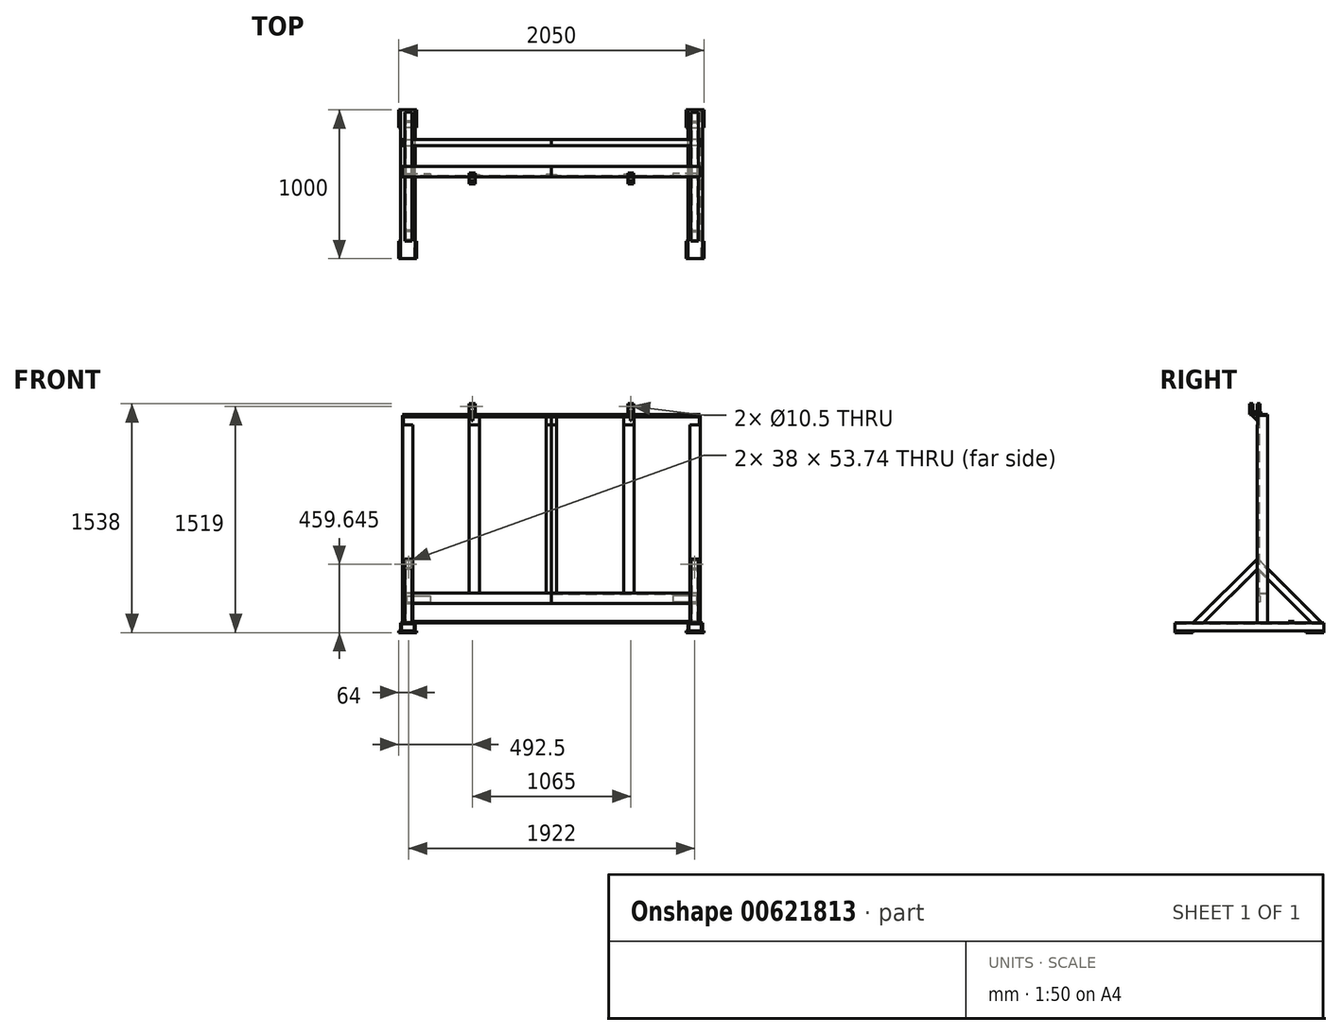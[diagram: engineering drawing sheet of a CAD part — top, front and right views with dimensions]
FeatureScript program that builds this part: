
annotation { "Feature Type Name" : "Feature", "Feature Type Description" : "" }
export const myFeature = defineFeature(function(context is Context, id is Id, definition is map)
    precondition{}
    {
        {
            var Q0;
            Q0=qCreatedBy(makeId("Front.planeOp"),FACE);
            var sketch = newSketch(context, id + "F0", { "sketchPlane" : qUnion([Q0])});
            skLineSegment(sketch, "E0", {"start": v(-915, 0) * mm, "end": v(-915, 53) * mm});
            skLineSegment(sketch, "E1", {"start": v(-915, 53) * mm, "end": v(-1015, 53) * mm});
            skLineSegment(sketch, "E2", {"start": v(-1015, 53) * mm, "end": v(-1015, 0) * mm});
            skLineSegment(sketch, "E3", {"start": v(-1015, 0) * mm, "end": v(-1007, 0) * mm});
            skLineSegment(sketch, "E4", {"start": v(-1007, 0) * mm, "end": v(-1007, 47) * mm});
            skLineSegment(sketch, "E5", {"start": v(-1007, 47) * mm, "end": v(-923, 47) * mm});
            skLineSegment(sketch, "E6", {"start": v(-923, 47) * mm, "end": v(-923, 0) * mm});
            skLineSegment(sketch, "E7", {"start": v(-923, 0) * mm, "end": v(-915, 0) * mm});
            skLineSegment(sketch, "E8", {"start": v(0, 0) * mm, "end": v(0, 53) * mm, "construction": true});
            skSolve(sketch);
        }
        {
            var Q0;
            Q0=qSketchRegion(id+"F0",true);
            extrude(context, id + "F1", {"entities" : qUnion([Q0]), "depth" : 1000 * mm, "hasSecondDirection" : true, "secondDirectionOppositeDirection" : true, "secondDirectionDepth" : 500 * mm, "symmetric" : true});
        }
        {
            var Q0;
            Q0=makeQuery(id+"F1.opExtrude","SWEPT_FACE",FACE,{"disambiguationData":[OSD([sQuery(id+"F0.wireOp",EDGE,"E1")])]});
            var sketch = newSketch(context, id + "F2", { "sketchPlane" : qUnion([Q0])});
            skLineSegment(sketch, "E9", {"start": v(-965, -500) * mm, "end": v(-965, 500) * mm, "construction": true});
            skLineSegment(sketch, "E10", {"start": v(-930, 50) * mm, "end": v(-1000, 50) * mm});
            skLineSegment(sketch, "E11", {"start": v(-1000, 50) * mm, "end": v(-1000, 120) * mm});
            skLineSegment(sketch, "E12", {"start": v(-1000, 120) * mm, "end": v(-994, 120) * mm});
            skLineSegment(sketch, "E13", {"start": v(-994, 120) * mm, "end": v(-994, 56) * mm});
            skLineSegment(sketch, "E14", {"start": v(-994, 56) * mm, "end": v(-930, 56) * mm});
            skLineSegment(sketch, "E15", {"start": v(-930, 56) * mm, "end": v(-930, 50) * mm});
            skSolve(sketch);
        }
        {
            var Q0;
            Q0=qSketchRegion(id+"F2",true);
            extrude(context, id + "F3", {"entities" : qUnion([Q0]), "depth" : 1400 * mm});
        }
        {
            var Q0;
            Q0=makeQuery(id+"F3.opExtrude","SWEPT_FACE",FACE,{"disambiguationData":[OSD([sQuery(id+"F2.wireOp",EDGE,"E10")])]});
            var sketch = newSketch(context, id + "F4", { "sketchPlane" : qUnion([Q0])});
            skLineSegment(sketch, "E16", {"start": v(-1000, 1453) * mm, "end": v(-930, 1383) * mm});
            skLineSegment(sketch, "E17", {"start": v(-930, 1383) * mm, "end": v(-930, 1453) * mm});
            skLineSegment(sketch, "E18", {"start": v(-930, 1453) * mm, "end": v(-1000, 1453) * mm});
            skSolve(sketch);
        }
        {
            var Q0;
            Q0=makeQuery(id+"F4.imprint","IMPRINT",FACE,{"disambiguationData":[TD([[makeQuery(id+"F4.imprint","IMPRINT",EDGE,{"derivedFrom":sQuery(id+"F4.wireOp",EDGE,"E16")}),1.0]])]});
            extrude(context, id + "F5", {"entities" : qUnion([Q0]), "operationType" : NewBodyOperationType.REMOVE, "endBound" : BoundingType.UP_TO_NEXT, "oppositeDirection" : true, "depth" : 25 * mm});
        }
        {
            var Q0;
            Q0=makeQuery(id+"F3.opExtrude","SWEPT_FACE",FACE,{"disambiguationData":[OSD([sQuery(id+"F2.wireOp",EDGE,"E11")])]});
            var sketch = newSketch(context, id + "F6", { "sketchPlane" : qUnion([Q0])});
            skLineSegment(sketch, "E19", {"start": v(-120, 1453) * mm, "end": v(-50, 1453) * mm});
            skLineSegment(sketch, "E20", {"start": v(-50, 1453) * mm, "end": v(-50, 1383) * mm});
            skLineSegment(sketch, "E21", {"start": v(-50, 1383) * mm, "end": v(-56, 1383) * mm});
            skLineSegment(sketch, "E22", {"start": v(-56, 1383) * mm, "end": v(-56, 1447) * mm});
            skLineSegment(sketch, "E23", {"start": v(-56, 1447) * mm, "end": v(-120, 1447) * mm});
            skLineSegment(sketch, "E24", {"start": v(-120, 1447) * mm, "end": v(-120, 1453) * mm});
            skSolve(sketch);
        }
        {
            var Q0;
            Q0=makeQuery(id+"F6.imprint","IMPRINT",FACE,{"disambiguationData":[TD([[makeQuery(id+"F6.imprint","IMPRINT",EDGE,{"derivedFrom":sQuery(id+"F6.wireOp",EDGE,"E19")}),1.0]])]});
            var Q1;
            Q1=qCreatedBy(makeId("Right.planeOp"),FACE);
            extrude(context, id + "F7", {"entities" : qUnion([Q0]), "endBound" : BoundingType.UP_TO_SURFACE, "oppositeDirection" : true, "endBoundEntityFace" : qUnion([Q1]), "depth" : 1105 * mm});
        }
        {
            var Q0;
            Q0=makeQuery(id+"F7.opExtrude","SWEPT_FACE",FACE,{"disambiguationData":[OSD([sQuery(id+"F6.wireOp",EDGE,"E20")])]});
            var sketch = newSketch(context, id + "F8", { "sketchPlane" : qUnion([Q0])});
            skLineSegment(sketch, "E25", {"start": v(-1000, 1453) * mm, "end": v(-1000, 1383) * mm});
            skLineSegment(sketch, "E26", {"start": v(-1000, 1383) * mm, "end": v(-930, 1383) * mm});
            skLineSegment(sketch, "E27", {"start": v(-930, 1383) * mm, "end": v(-1000, 1453) * mm});
            skSolve(sketch);
        }
        {
            var Q0;
            Q0=makeQuery(id+"F8.imprint","IMPRINT",FACE,{"disambiguationData":[TD([[makeQuery(id+"F8.imprint","IMPRINT",EDGE,{"derivedFrom":sQuery(id+"F8.wireOp",EDGE,"E25")}),1.0]])]});
            extrude(context, id + "F9", {"entities" : qUnion([Q0]), "operationType" : NewBodyOperationType.REMOVE, "endBound" : BoundingType.UP_TO_NEXT, "oppositeDirection" : true, "depth" : 25 * mm});
        }
        {
            var Q0;
            Q0=makeQuery(id+"F3.opExtrude","SWEPT_FACE",FACE,{"disambiguationData":[OSD([sQuery(id+"F2.wireOp",EDGE,"E13")])]});
            cPlane(context, id + "F10", {"entities" : qUnion([Q0]), "cplaneType" : CPlaneType.OFFSET, "offset" : 8 * mm, "width" : 150 * mm, "height" : 150 * mm});
        }
        {
            var Q0;
            Q0=qCreatedBy(id+"F10.planeOp",FACE);
            var sketch = newSketch(context, id + "F11", { "sketchPlane" : qUnion([Q0])});
            skLineSegment(sketch, "E28", {"start": v(56, 483) * mm, "end": v(56, 412.29) * mm});
            skLineSegment(sketch, "E29", {"start": v(56, 412.29) * mm, "end": v(415.29, 53) * mm});
            skLineSegment(sketch, "E30", {"start": v(415.29, 53) * mm, "end": v(486, 53) * mm});
            skLineSegment(sketch, "E31", {"start": v(486, 53) * mm, "end": v(56, 483) * mm});
            skLineSegment(sketch, "E32", {"start": v(50, 483) * mm, "end": v(-380, 53) * mm});
            skLineSegment(sketch, "E33", {"start": v(-380, 53) * mm, "end": v(-309.29, 53) * mm});
            skLineSegment(sketch, "E34", {"start": v(-309.29, 53) * mm, "end": v(50, 412.29) * mm});
            skLineSegment(sketch, "E35", {"start": v(50, 412.29) * mm, "end": v(50, 483) * mm});
            skSolve(sketch);
        }
        {
            var Q0;
            Q0=qSketchRegion(id+"F11",true);
            extrude(context, id + "F12", {"entities" : qUnion([Q0]), "depth" : 50 * mm});
        }
        {
            var Q0;
            Q0=makeQuery(id+"F12.opExtrude","SWEPT_FACE",FACE,{"disambiguationData":[OSD([sQuery(id+"F11.wireOp",EDGE,"E33")])]});
            var Q1;
            Q1=makeQuery(id+"F12.opExtrude","SWEPT_FACE",FACE,{"disambiguationData":[OSD([sQuery(id+"F11.wireOp",EDGE,"E30")])]});
            var Q2;
            Q2=makeQuery(id+"F12.opExtrude","SWEPT_FACE",FACE,{"disambiguationData":[OSD([sQuery(id+"F11.wireOp",EDGE,"E28")])]});
            var Q3;
            Q3=makeQuery(id+"F12.opExtrude","SWEPT_FACE",FACE,{"disambiguationData":[OSD([sQuery(id+"F11.wireOp",EDGE,"E35")])]});
            shell(context, id + "F13", {"entities" : qUnion([Q0, Q1, Q2, Q3]), "thickness" : 6 * mm});
        }
        {
            var Q0;
            Q0=makeQuery(id+"F3.opExtrude","SWEPT_FACE",FACE,{"disambiguationData":[OSD([sQuery(id+"F2.wireOp",EDGE,"E13")])]});
            var sketch = newSketch(context, id + "F14", { "sketchPlane" : qUnion([Q0])});
            skLineSegment(sketch, "E36", {"start": v(50, 253) * mm, "end": v(120, 253) * mm});
            skLineSegment(sketch, "E37", {"start": v(120, 253) * mm, "end": v(120, 247) * mm});
            skLineSegment(sketch, "E38", {"start": v(120, 247) * mm, "end": v(56, 247) * mm});
            skLineSegment(sketch, "E39", {"start": v(56, 247) * mm, "end": v(56, 183) * mm});
            skLineSegment(sketch, "E40", {"start": v(56, 183) * mm, "end": v(50, 183) * mm});
            skLineSegment(sketch, "E41", {"start": v(50, 183) * mm, "end": v(50, 253) * mm});
            skSolve(sketch);
        }
        {
            var Q0;
            {var subQ1=sQuery(id+"F14.wireOp",EDGE,"E39");Q0=makeQuery(id+"F14.imprint","IMPRINT",FACE,{"disambiguationData":[TD([[makeQuery(id+"F14.imprint","IMPRINT",EDGE,{"derivedFrom":subQ1}),-1.0]])]});}
            var Q1;
            {var subQ0=sQuery(id+"F14.wireOp",EDGE,"E37");Q1=makeQuery(id+"F14.imprint","IMPRINT",FACE,{"disambiguationData":[TD([[makeQuery(id+"F14.imprint","IMPRINT",EDGE,{"derivedFrom":subQ0}),-1.0]])]});}
            var Q2;
            Q2=qCreatedBy(makeId("Right.planeOp"),FACE);
            var Q3;
            Q3=makeQuery(id+"F7.opExtrude","SWEPT_BODY",BODY,{"disambiguationData":[OSD([sQuery(id+"F6.wireOp",EDGE,"E19"),sQuery(id+"F6.wireOp",EDGE,"E20"),sQuery(id+"F6.wireOp",EDGE,"E21"),sQuery(id+"F6.wireOp",EDGE,"E22"),sQuery(id+"F6.wireOp",EDGE,"E23"),sQuery(id+"F6.wireOp",EDGE,"E24")])]});
            extrude(context, id + "F15", {"entities" : qUnion([Q0, Q1]), "endBound" : BoundingType.UP_TO_SURFACE, "endBoundEntityFace" : qUnion([Q2]), "endBoundEntityBody" : qUnion([Q3]), "depth" : 1005 * mm});
        }
        {
            var Q0;
            Q0=makeQuery(id+"F15.opExtrude","SWEPT_FACE",FACE,{"disambiguationData":[OSD([sQuery(id+"F14.wireOp",EDGE,"E41")])]});
            var sketch = newSketch(context, id + "F16", { "sketchPlane" : qUnion([Q0])});
            skLineSegment(sketch, "E42.bottom", {"start": v(-994, 253) * mm, "end": v(-930, 253) * mm});
            skLineSegment(sketch, "E42.top", {"start": v(-994, 183) * mm, "end": v(-930, 183) * mm});
            skLineSegment(sketch, "E42.left", {"start": v(-994, 253) * mm, "end": v(-994, 183) * mm});
            skLineSegment(sketch, "E42.right", {"start": v(-930, 253) * mm, "end": v(-930, 183) * mm});
            skSolve(sketch);
        }
        {
            var Q0;
            Q0=makeQuery(id+"F16.imprint","IMPRINT",FACE,{"disambiguationData":[TD([[makeQuery(id+"F16.imprint","IMPRINT",EDGE,{"derivedFrom":sQuery(id+"F16.wireOp",EDGE,"E42.bottom")}),1.0]])]});
            extrude(context, id + "F17", {"entities" : qUnion([Q0]), "operationType" : NewBodyOperationType.REMOVE, "oppositeDirection" : true, "depth" : 70 * mm});
        }
        {
            var Q0;
            Q0=makeQuery(id+"F3.opExtrude","SWEPT_FACE",FACE,{"disambiguationData":[OSD([sQuery(id+"F2.wireOp",EDGE,"E14")])]});
            var sketch = newSketch(context, id + "F18", { "sketchPlane" : qUnion([Q0])});
            skLineSegment(sketch, "E43.bottom", {"start": v(974, 235) * mm, "end": v(814, 235) * mm});
            skLineSegment(sketch, "E43.top", {"start": v(974, 195) * mm, "end": v(814, 195) * mm});
            skLineSegment(sketch, "E43.left", {"start": v(974, 235) * mm, "end": v(974, 195) * mm});
            skLineSegment(sketch, "E43.right", {"start": v(814, 235) * mm, "end": v(814, 195) * mm});
            skLineSegment(sketch, "E44", {"start": v(814, 215) * mm, "end": v(974, 215) * mm, "construction": true});
            skSolve(sketch);
        }
        {
            var Q0;
            {var subQ0=sQuery(id+"F18.wireOp",EDGE,"E43.right");Q0=makeQuery(id+"F18.imprint","IMPRINT",FACE,{"disambiguationData":[TD([[makeQuery(id+"F18.imprint","IMPRINT",EDGE,{"derivedFrom":subQ0}),1.0]])]});}
            var Q1;
            {var subQ0=sQuery(id+"F18.wireOp",EDGE,"E43.left");Q1=makeQuery(id+"F18.imprint","IMPRINT",FACE,{"disambiguationData":[TD([[makeQuery(id+"F18.imprint","IMPRINT",EDGE,{"derivedFrom":subQ0}),-1.0]])]});}
            extrude(context, id + "F19", {"entities" : qUnion([Q0, Q1]), "depth" : 15 * mm});
        }
        {
            var Q0;
            Q0=makeQuery(id+"F7.opExtrude","SWEPT_FACE",FACE,{"disambiguationData":[OSD([sQuery(id+"F6.wireOp",EDGE,"E20")])]});
            var sketch = newSketch(context, id + "F20", { "sketchPlane" : qUnion([Q0])});
            skLineSegment(sketch, "E45.bottom", {"start": v(0, 1438) * mm, "end": v(-35, 1438) * mm});
            skLineSegment(sketch, "E45.top", {"start": v(0, 253) * mm, "end": v(-35, 253) * mm});
            skLineSegment(sketch, "E45.left", {"start": v(0, 1438) * mm, "end": v(0, 253) * mm});
            skLineSegment(sketch, "E45.right", {"start": v(-35, 1438) * mm, "end": v(-35, 253) * mm});
            skLineSegment(sketch, "E46.bottom", {"start": v(-555, 1438) * mm, "end": v(-485, 1438) * mm});
            skLineSegment(sketch, "E46.top", {"start": v(-555, 253) * mm, "end": v(-485, 253) * mm});
            skLineSegment(sketch, "E46.left", {"start": v(-555, 1438) * mm, "end": v(-555, 253) * mm});
            skLineSegment(sketch, "E46.right", {"start": v(-485, 1438) * mm, "end": v(-485, 253) * mm});
            skSolve(sketch);
        }
        {
            var Q0;
            {var subQ0=sQuery(id+"F20.wireOp",EDGE,"E46.bottom");Q0=makeQuery(id+"F20.imprint","IMPRINT",FACE,{"disambiguationData":[TD([[makeQuery(id+"F20.imprint","IMPRINT",EDGE,{"derivedFrom":subQ0}),-1.0]])]});}
            var Q1;
            {var subQ0=sQuery(id+"F20.wireOp",EDGE,"E46.top");Q1=makeQuery(id+"F20.imprint","IMPRINT",FACE,{"disambiguationData":[TD([[makeQuery(id+"F20.imprint","IMPRINT",EDGE,{"derivedFrom":subQ0}),1.0]])]});}
            var Q2;
            {var subQ0=sQuery(id+"F20.wireOp",EDGE,"E45.bottom");Q2=makeQuery(id+"F20.imprint","IMPRINT",FACE,{"disambiguationData":[TD([[makeQuery(id+"F20.imprint","IMPRINT",EDGE,{"derivedFrom":subQ0}),1.0]])]});}
            var Q3;
            {var subQ0=sQuery(id+"F20.wireOp",EDGE,"E45.top");Q3=makeQuery(id+"F20.imprint","IMPRINT",FACE,{"disambiguationData":[TD([[makeQuery(id+"F20.imprint","IMPRINT",EDGE,{"derivedFrom":subQ0}),-1.0]])]});}
            extrude(context, id + "F21", {"entities" : qUnion([Q0, Q1, Q2, Q3]), "oppositeDirection" : true, "depth" : 15 * mm});
        }
        {
            var Q0;
            Q0=makeQuery(id+"F21.opExtrude","SWEPT_FACE",FACE,{"disambiguationData":[OSD([sQuery(id+"F20.wireOp",EDGE,"E45.left")])]});
            var sketch = newSketch(context, id + "F22", { "sketchPlane" : qUnion([Q0])});
            skLineSegment(sketch, "E47.bottom", {"start": v(56, 1438) * mm, "end": v(50, 1438) * mm});
            skLineSegment(sketch, "E47.top", {"start": v(56, 1383) * mm, "end": v(50, 1383) * mm});
            skLineSegment(sketch, "E47.left", {"start": v(56, 1438) * mm, "end": v(56, 1383) * mm});
            skLineSegment(sketch, "E47.right", {"start": v(50, 1438) * mm, "end": v(50, 1383) * mm});
            skSolve(sketch);
        }
        {
            var Q0;
            Q0=makeQuery(id+"F22.imprint","IMPRINT",FACE,{"disambiguationData":[TD([[makeQuery(id+"F22.imprint","IMPRINT",EDGE,{"derivedFrom":sQuery(id+"F22.wireOp",EDGE,"E47.bottom")}),1.0]])]});
            extrude(context, id + "F23", {"entities" : qUnion([Q0]), "operationType" : NewBodyOperationType.REMOVE, "oppositeDirection" : true, "depth" : 1000 * mm});
        }
        {
            var Q0;
            Q0=makeQuery(id+"F1.opExtrude","SWEPT_FACE",FACE,{"disambiguationData":[OSD([sQuery(id+"F0.wireOp",EDGE,"E1")])]});
            var sketch = newSketch(context, id + "F24", { "sketchPlane" : qUnion([Q0])});
            skLineSegment(sketch, "E48.bottom", {"start": v(-1005, 260) * mm, "end": v(0, 260) * mm});
            skLineSegment(sketch, "E48.top", {"start": v(-1005, 300) * mm, "end": v(0, 300) * mm});
            skLineSegment(sketch, "E48.left", {"start": v(-1005, 260) * mm, "end": v(-1005, 300) * mm});
            skLineSegment(sketch, "E48.right", {"start": v(0, 260) * mm, "end": v(0, 300) * mm});
            skSolve(sketch);
        }
        {
            var Q0;
            {var subQ0=sQuery(id+"F24.wireOp",EDGE,"E48.right");Q0=makeQuery(id+"F24.imprint","IMPRINT",FACE,{"disambiguationData":[TD([[makeQuery(id+"F24.imprint","IMPRINT",EDGE,{"derivedFrom":subQ0}),1.0]])]});}
            var Q1;
            {var subQ0=sQuery(id+"F24.wireOp",EDGE,"E48.left");Q1=makeQuery(id+"F24.imprint","IMPRINT",FACE,{"disambiguationData":[TD([[makeQuery(id+"F24.imprint","IMPRINT",EDGE,{"derivedFrom":subQ0}),-1.0]])]});}
            extrude(context, id + "F25", {"entities" : qUnion([Q0, Q1]), "depth" : 12 * mm});
        }
        {
            var Q0;
            Q0=makeQuery(id+"F7.opExtrude","SWEPT_FACE",FACE,{"disambiguationData":[OSD([sQuery(id+"F6.wireOp",EDGE,"E19")])]});
            var sketch = newSketch(context, id + "F26", { "sketchPlane" : qUnion([Q0])});
            skLineSegment(sketch, "E49.bottom", {"start": v(-552.5, 77) * mm, "end": v(-512.5, 77) * mm});
            skLineSegment(sketch, "E49.top", {"start": v(-552.5, 2) * mm, "end": v(-512.5, 2) * mm});
            skLineSegment(sketch, "E49.left", {"start": v(-552.5, 77) * mm, "end": v(-552.5, 2) * mm});
            skLineSegment(sketch, "E49.right", {"start": v(-512.5, 77) * mm, "end": v(-512.5, 2) * mm});
            skSolve(sketch);
        }
        {
            var Q0;
            Q0=qSketchRegion(id+"F26",true);
            extrude(context, id + "F27", {"entities" : qUnion([Q0]), "depth" : 20 * mm});
        }
        {
            var Q0;
            Q0=makeQuery(id+"F27.opExtrude","CAP_FACE",FACE,{"disambiguationData":[OSD([sQuery(id+"F26.wireOp",EDGE,"E49.bottom"),sQuery(id+"F26.wireOp",EDGE,"E49.top"),sQuery(id+"F26.wireOp",EDGE,"E49.left"),sQuery(id+"F26.wireOp",EDGE,"E49.right")])],"isStart":false});
            var sketch = newSketch(context, id + "F28", { "sketchPlane" : qUnion([Q0])});
            skLineSegment(sketch, "E50.bottom", {"start": v(-552.5, 2) * mm, "end": v(-512.5, 2) * mm});
            skLineSegment(sketch, "E50.top", {"start": v(-552.5, 22) * mm, "end": v(-512.5, 22) * mm});
            skLineSegment(sketch, "E50.left", {"start": v(-552.5, 2) * mm, "end": v(-552.5, 22) * mm});
            skLineSegment(sketch, "E50.right", {"start": v(-512.5, 2) * mm, "end": v(-512.5, 22) * mm});
            skLineSegment(sketch, "E51.bottom", {"start": v(-552.5, 50) * mm, "end": v(-512.5, 50) * mm});
            skLineSegment(sketch, "E51.top", {"start": v(-552.5, 70) * mm, "end": v(-512.5, 70) * mm});
            skLineSegment(sketch, "E51.left", {"start": v(-552.5, 50) * mm, "end": v(-552.5, 70) * mm});
            skLineSegment(sketch, "E51.right", {"start": v(-512.5, 50) * mm, "end": v(-512.5, 70) * mm});
            skSolve(sketch);
        }
        {
            var Q0;
            Q0=qSketchRegion(id+"F28",true);
            extrude(context, id + "F29", {"entities" : qUnion([Q0]), "depth" : 53 * mm});
        }
        {
            var Q0;
            Q0=makeQuery(id+"F27.opExtrude","SWEPT_FACE",FACE,{"disambiguationData":[OSD([sQuery(id+"F26.wireOp",EDGE,"E49.left")])]});
            var Q1;
            Q1=makeQuery(id+"F27.opExtrude","SWEPT_FACE",FACE,{"disambiguationData":[OSD([sQuery(id+"F26.wireOp",EDGE,"E49.right")])]});
            cPlane(context, id + "F30", {"entities" : qUnion([Q0, Q1]), "cplaneType" : CPlaneType.MID_PLANE, "offset" : 25 * mm, "width" : 150 * mm, "height" : 150 * mm});
        }
        {
            var Q0;
            Q0=qCreatedBy(id+"F30.planeOp",FACE);
            var sketch = newSketch(context, id + "F31", { "sketchPlane" : qUnion([Q0])});
            skLineSegment(sketch, "E52", {"start": v(-10, 1453) * mm, "end": v(-50, 1413) * mm});
            skLineSegment(sketch, "E53", {"start": v(-50, 1413) * mm, "end": v(-50, 1453) * mm});
            skLineSegment(sketch, "E54", {"start": v(-50, 1453) * mm, "end": v(-10, 1453) * mm});
            skSolve(sketch);
        }
        {
            var Q0;
            Q0=qSketchRegion(id+"F31",true);
            extrude(context, id + "F32", {"entities" : qUnion([Q0]), "depth" : 8 * mm, "symmetric" : true});
        }
        {
            var Q0;
            Q0=makeQuery(id+"F29.opExtrude","SWEPT_FACE",FACE,{"disambiguationData":[OSD([sQuery(id+"F28.wireOp",EDGE,"E50.bottom")])]});
            var sketch = newSketch(context, id + "F33", { "sketchPlane" : qUnion([Q0])});
            skLineSegment(sketch, "E55", {"start": v(-532.5, 1526) * mm, "end": v(-532.5, 1473) * mm, "construction": true});
            skPoint(sketch, "E56", {"position": v(-532.5, 1507) * mm});
            skSolve(sketch);
        }
        {
            var Q0;
            Q0=sQuery(id+"F33.wireOp",VERTEX,"E56");
            var Q1;
            Q1=makeQuery(id+"F29.opExtrude","SWEPT_BODY",BODY,{"disambiguationData":[OSD([sQuery(id+"F28.wireOp",EDGE,"E50.bottom"),sQuery(id+"F28.wireOp",EDGE,"E50.top"),sQuery(id+"F28.wireOp",EDGE,"E50.left"),sQuery(id+"F28.wireOp",EDGE,"E50.right")])]});
            hole(context, id + "F34", {"style" : HoleStyle.SIMPLE, "endStyle" : HoleEndStyle.THROUGH, "standardTappedOrClearance" : lookupTablePath({ "standard" : "ISO", "engagement" : "75%", "pitch" : "1.5 mm", "size" : "M12", "type" : "Tapped" }), "standardBlindInLast" : lookupTablePath({ "standard" : "ISO", "engagement" : "75%", "pitch" : "1.5 mm", "size" : "M12", "type" : "Tapped" }), "holeDiameter" : 10.5 * mm, "locations" : qUnion([Q0]), "scope" : qUnion([Q1]), "isTappedThrough" : true, "majorDiameter" : 12 * mm, "showTappedDepth" : true});
        }
        {
            var Q0;
            Q0=makeQuery(id+"F1.opExtrude","SWEPT_FACE",FACE,{"disambiguationData":[OSD([sQuery(id+"F0.wireOp",EDGE,"E3")])]});
            var sketch = newSketch(context, id + "F35", { "sketchPlane" : qUnion([Q0])});
            skLineSegment(sketch, "E57.bottom", {"start": v(-905, -380) * mm, "end": v(-1025, -380) * mm});
            skLineSegment(sketch, "E57.top", {"start": v(-905, -500) * mm, "end": v(-1025, -500) * mm});
            skLineSegment(sketch, "E57.left", {"start": v(-905, -380) * mm, "end": v(-905, -500) * mm});
            skLineSegment(sketch, "E57.right", {"start": v(-1025, -380) * mm, "end": v(-1025, -500) * mm});
            skLineSegment(sketch, "E58", {"start": v(-965, -380) * mm, "end": v(-965, -500) * mm, "construction": true});
            skLineSegment(sketch, "E59", {"start": v(-1007, 0) * mm, "end": v(-923, 0) * mm, "construction": true});
            skPoint(sketch, "E59.endSnap0", {"position": v(-1007, 0) * mm});
            skLineSegment(sketch, "E60.MirrorCS", {"start": v(-905, 380) * mm, "end": v(-1025, 380) * mm});
            skLineSegment(sketch, "E61.MirrorCS", {"start": v(-905, 380) * mm, "end": v(-905, 500) * mm});
            skLineSegment(sketch, "E62.MirrorCS", {"start": v(-905, 500) * mm, "end": v(-1025, 500) * mm});
            skLineSegment(sketch, "E63.MirrorCS", {"start": v(-1025, 380) * mm, "end": v(-1025, 500) * mm});
            skLineSegment(sketch, "E64.MirrorCS", {"start": v(-965, 380) * mm, "end": v(-965, 500) * mm, "construction": true});
            skSolve(sketch);
        }
        {
            var Q0;
            Q0=qSketchRegion(id+"F35",true);
            extrude(context, id + "F36", {"entities" : qUnion([Q0]), "depth" : 12 * mm});
        }
        {
            var Q0;
            Q0=makeQuery(id+"F1.opExtrude","SWEPT_BODY",BODY,{"disambiguationData":[OSD([sQuery(id+"F0.wireOp",EDGE,"E0"),sQuery(id+"F0.wireOp",EDGE,"E1"),sQuery(id+"F0.wireOp",EDGE,"E2"),sQuery(id+"F0.wireOp",EDGE,"E3"),sQuery(id+"F0.wireOp",EDGE,"E4"),sQuery(id+"F0.wireOp",EDGE,"E5"),sQuery(id+"F0.wireOp",EDGE,"E6"),sQuery(id+"F0.wireOp",EDGE,"E7")])]});
            var Q1;
            Q1=makeQuery(id+"F12.opExtrude","SWEPT_BODY",BODY,{"disambiguationData":[OSD([sQuery(id+"F11.wireOp",EDGE,"E28"),sQuery(id+"F11.wireOp",EDGE,"E29"),sQuery(id+"F11.wireOp",EDGE,"E30"),sQuery(id+"F11.wireOp",EDGE,"E31")])]});
            var Q2;
            Q2=makeQuery(id+"F12.opExtrude","SWEPT_BODY",BODY,{"disambiguationData":[OSD([sQuery(id+"F11.wireOp",EDGE,"E32"),sQuery(id+"F11.wireOp",EDGE,"E33"),sQuery(id+"F11.wireOp",EDGE,"E34"),sQuery(id+"F11.wireOp",EDGE,"E35")])]});
            var Q3;
            Q3=makeQuery(id+"F15.opExtrude","SWEPT_BODY",BODY,{"disambiguationData":[OSD([sQuery(id+"F14.wireOp",EDGE,"E36"),sQuery(id+"F14.wireOp",EDGE,"E37"),sQuery(id+"F14.wireOp",EDGE,"E38"),sQuery(id+"F14.wireOp",EDGE,"E39"),sQuery(id+"F14.wireOp",EDGE,"E40"),sQuery(id+"F14.wireOp",EDGE,"E41")])]});
            var Q4;
            Q4=makeQuery(id+"F21.opExtrude","SWEPT_BODY",BODY,{"disambiguationData":[OSD([sQuery(id+"F20.wireOp",EDGE,"E46.bottom"),sQuery(id+"F20.wireOp",EDGE,"E46.top"),sQuery(id+"F20.wireOp",EDGE,"E46.left"),sQuery(id+"F20.wireOp",EDGE,"E46.right")])]});
            var Q5;
            Q5=makeQuery(id+"F21.opExtrude","SWEPT_BODY",BODY,{"disambiguationData":[OSD([sQuery(id+"F20.wireOp",EDGE,"E45.bottom"),sQuery(id+"F20.wireOp",EDGE,"E45.top"),sQuery(id+"F20.wireOp",EDGE,"E45.left"),sQuery(id+"F20.wireOp",EDGE,"E45.right")])]});
            var Q6;
            Q6=makeQuery(id+"F3.opExtrude","SWEPT_BODY",BODY,{"disambiguationData":[OSD([sQuery(id+"F2.wireOp",EDGE,"E10"),sQuery(id+"F2.wireOp",EDGE,"E11"),sQuery(id+"F2.wireOp",EDGE,"E12"),sQuery(id+"F2.wireOp",EDGE,"E13"),sQuery(id+"F2.wireOp",EDGE,"E14"),sQuery(id+"F2.wireOp",EDGE,"E15")])]});
            var Q7;
            Q7=makeQuery(id+"F7.opExtrude","SWEPT_BODY",BODY,{"disambiguationData":[OSD([sQuery(id+"F6.wireOp",EDGE,"E19"),sQuery(id+"F6.wireOp",EDGE,"E20"),sQuery(id+"F6.wireOp",EDGE,"E21"),sQuery(id+"F6.wireOp",EDGE,"E22"),sQuery(id+"F6.wireOp",EDGE,"E23"),sQuery(id+"F6.wireOp",EDGE,"E24")])]});
            var Q8;
            Q8=makeQuery(id+"F19.opExtrude","SWEPT_BODY",BODY,{"disambiguationData":[OSD([sQuery(id+"F18.wireOp",EDGE,"E43.bottom"),sQuery(id+"F18.wireOp",EDGE,"E43.top"),sQuery(id+"F18.wireOp",EDGE,"E43.left"),sQuery(id+"F18.wireOp",EDGE,"E43.right")])]});
            var Q9;
            Q9=makeQuery(id+"F27.opExtrude","SWEPT_BODY",BODY,{"disambiguationData":[OSD([sQuery(id+"F26.wireOp",EDGE,"E49.bottom"),sQuery(id+"F26.wireOp",EDGE,"E49.top"),sQuery(id+"F26.wireOp",EDGE,"E49.left"),sQuery(id+"F26.wireOp",EDGE,"E49.right")])]});
            var Q10;
            Q10=makeQuery(id+"F29.opExtrude","SWEPT_BODY",BODY,{"disambiguationData":[OSD([sQuery(id+"F28.wireOp",EDGE,"E51.bottom"),sQuery(id+"F28.wireOp",EDGE,"E51.top"),sQuery(id+"F28.wireOp",EDGE,"E51.left"),sQuery(id+"F28.wireOp",EDGE,"E51.right")])]});
            var Q11;
            Q11=makeQuery(id+"F29.opExtrude","SWEPT_BODY",BODY,{"disambiguationData":[OSD([sQuery(id+"F28.wireOp",EDGE,"E50.bottom"),sQuery(id+"F28.wireOp",EDGE,"E50.top"),sQuery(id+"F28.wireOp",EDGE,"E50.left"),sQuery(id+"F28.wireOp",EDGE,"E50.right")])]});
            var Q12;
            Q12=makeQuery(id+"F32.opExtrude","SWEPT_BODY",BODY,{"disambiguationData":[OSD([sQuery(id+"F31.wireOp",EDGE,"E52"),sQuery(id+"F31.wireOp",EDGE,"E53"),sQuery(id+"F31.wireOp",EDGE,"E54")])]});
            var Q13;
            Q13=makeQuery(id+"F36.opExtrude","SWEPT_BODY",BODY,{"disambiguationData":[OSD([sQuery(id+"F35.wireOp",EDGE,"E57.bottom"),sQuery(id+"F35.wireOp",EDGE,"E57.top"),sQuery(id+"F35.wireOp",EDGE,"E57.left"),sQuery(id+"F35.wireOp",EDGE,"E57.right")])]});
            var Q14;
            Q14=makeQuery(id+"F36.opExtrude","SWEPT_BODY",BODY,{"disambiguationData":[OSD([sQuery(id+"F35.wireOp",EDGE,"E60.MirrorCS"),sQuery(id+"F35.wireOp",EDGE,"E61.MirrorCS"),sQuery(id+"F35.wireOp",EDGE,"E62.MirrorCS"),sQuery(id+"F35.wireOp",EDGE,"E63.MirrorCS")])]});
            var Q15;
            Q15=makeQuery(id+"F25.opExtrude","SWEPT_BODY",BODY,{"disambiguationData":[OSD([sQuery(id+"F24.wireOp",EDGE,"E48.bottom"),sQuery(id+"F24.wireOp",EDGE,"E48.top"),sQuery(id+"F24.wireOp",EDGE,"E48.left"),sQuery(id+"F24.wireOp",EDGE,"E48.right")])]});
            var Q16;
            Q16=qCreatedBy(makeId("Right.planeOp"),FACE);
            mirror(context, id + "F37", {"entities" : qUnion([Q0, Q1, Q2, Q3, Q4, Q5, Q6, Q7, Q8, Q9, Q10, Q11, Q12, Q13, Q14, Q15]), "mirrorPlane" : qUnion([Q16])});
        }
    });
